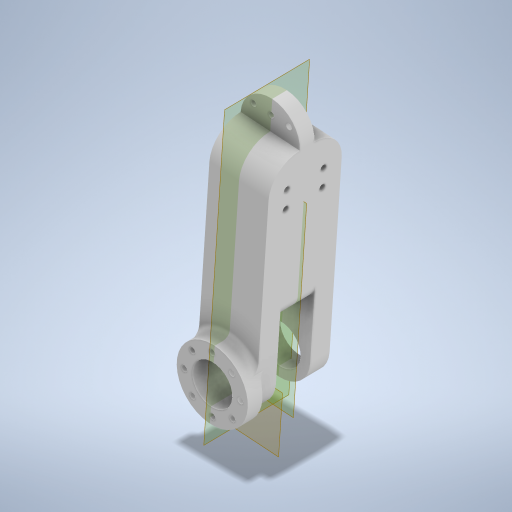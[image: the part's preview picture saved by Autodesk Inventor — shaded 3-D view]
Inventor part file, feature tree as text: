
AUTODESK INVENTOR PART (.ipt)
format: ipt  version: 2024 (Build 280153000, 153)  size: 751,616 bytes
history: native  units: mm
features: reference x14, extrude x7, sketch x7, projected_geometry x6, other x5, fillet x4, move_body x4, plane x3, direct_edit x3, mirror x1
ambient origin geometry x8: Origin, YZ Plane, XZ Plane, XY Plane, X Axis, Y Axis, Z Axis, Center Point
bodies: Solid1 (feature_tree)
feature tree (54):
  plane  "Work Plane1"
  extrude  "Extrusion1"  Depth=40.0mm
  plane  "Work Plane2"
  mirror  "Mirror1"
  extrude  "Extrusion2"  Depth=15.0mm TaperAngle=0.0deg
  extrude  "Extrusion3"  Depth=10.0mm TaperAngle=0.0deg
  fillet  "Fillet1"  Radius=10.0mm
  fillet  "Fillet2"  Radius=10.0mm
  extrude  "Extrusion4"  Depth=8.0mm
  extrude  "Extrusion5"  Depth=10.0mm TaperAngle=0.0deg
  fillet  "Fillet3"  Radius=4.0mm
  extrude  "Extrusion6"  Depth=8.0mm TaperAngle=0.0deg
  fillet  "Fillet4"  Radius=5.0mm
  direct_edit  "Direct Edit1"
  direct_edit  "Direct Edit2"
  direct_edit  "Direct Edit3"
  extrude  "Extrusion7"  Depth=8.0mm TaperAngle=0.0deg
  plane  "Work Plane3"
  sketch  "Sketch1"  dims[d0=40.0mm d1=40.0mm]
  reference  "Reference1"
  reference  "Reference2"
  reference  "Reference3"
  sketch  "Sketch2"  dims[d2=140.0mm d3=15.0mm d4=0.0mm]
  reference  "Reference4"
  projected_geometry  "Projected Loop1"
  sketch  "Sketch3"  dims[d5=10.0mm d10=15.0mm d11=0.0mm d12=10.0mm d13=10.0mm]
  projected_geometry  "Projected Loop2"
  sketch  "Sketch4"  dims[d14=10.0mm d15=8.0mm]
  reference  "Reference5"
  sketch  "Sketch5"  dims[d16=48.0mm d17=10.0mm d18=0.0mm d19=4.0mm]
  projected_geometry  "Projected Loop3"
  sketch  "Sketch6"  dims[d20=4.0mm d21=8.0mm d22=0.0mm d23=5.0mm]
  projected_geometry  "Projected Loop4"
  reference  "Reference6"
  reference  "Reference7"
  reference  "Reference8"
  reference  "Reference9"
  reference  "Reference10"
  reference  "Reference11"
  reference  "Reference12"
  projected_geometry  "Projected Loop5"
  reference  "Reference13"
  reference  "Reference14"
  sketch  "Sketch7"  dims[d24=20.0mm d25=8.0mm d26=0.0mm d27=20.0mm d28=3.9mm d29=12.0mm d30=12.0mm d31=10.0mm d32=20.0mm d33=0.0mm d34=0.0mm d35=20.0mm d36=0.0mm d37=0.0mm d38=-1.5mm d39=0.0mm d40=0.0mm d41=-1.5mm d42=0.0mm d43=0.0mm d44=-0.2mm d45=0.0mm d46=0.0mm d47=-0.2mm d48=3.9mm d53=12.5mm d54=0.0mm d55=12.0mm d57=12.0mm d60=0.0mm d61=0.0mm d62=12.5mm d63=12.5mm d64=12.5mm d65=20.0mm d66=20.0mm]
  projected_geometry  "Projected Loop6"
  other  "<userpath>\Documents\Inventor\robot arm\arms\arms.iam"
  other  "arms.iam"
  other  "arm-bearings:6"
  other  "arm middle:1"
  other  "upper arm pulley:1"
  move_body  "Move1"
  move_body  "Move2"
  move_body  "Move3"
  move_body  "Move4"
